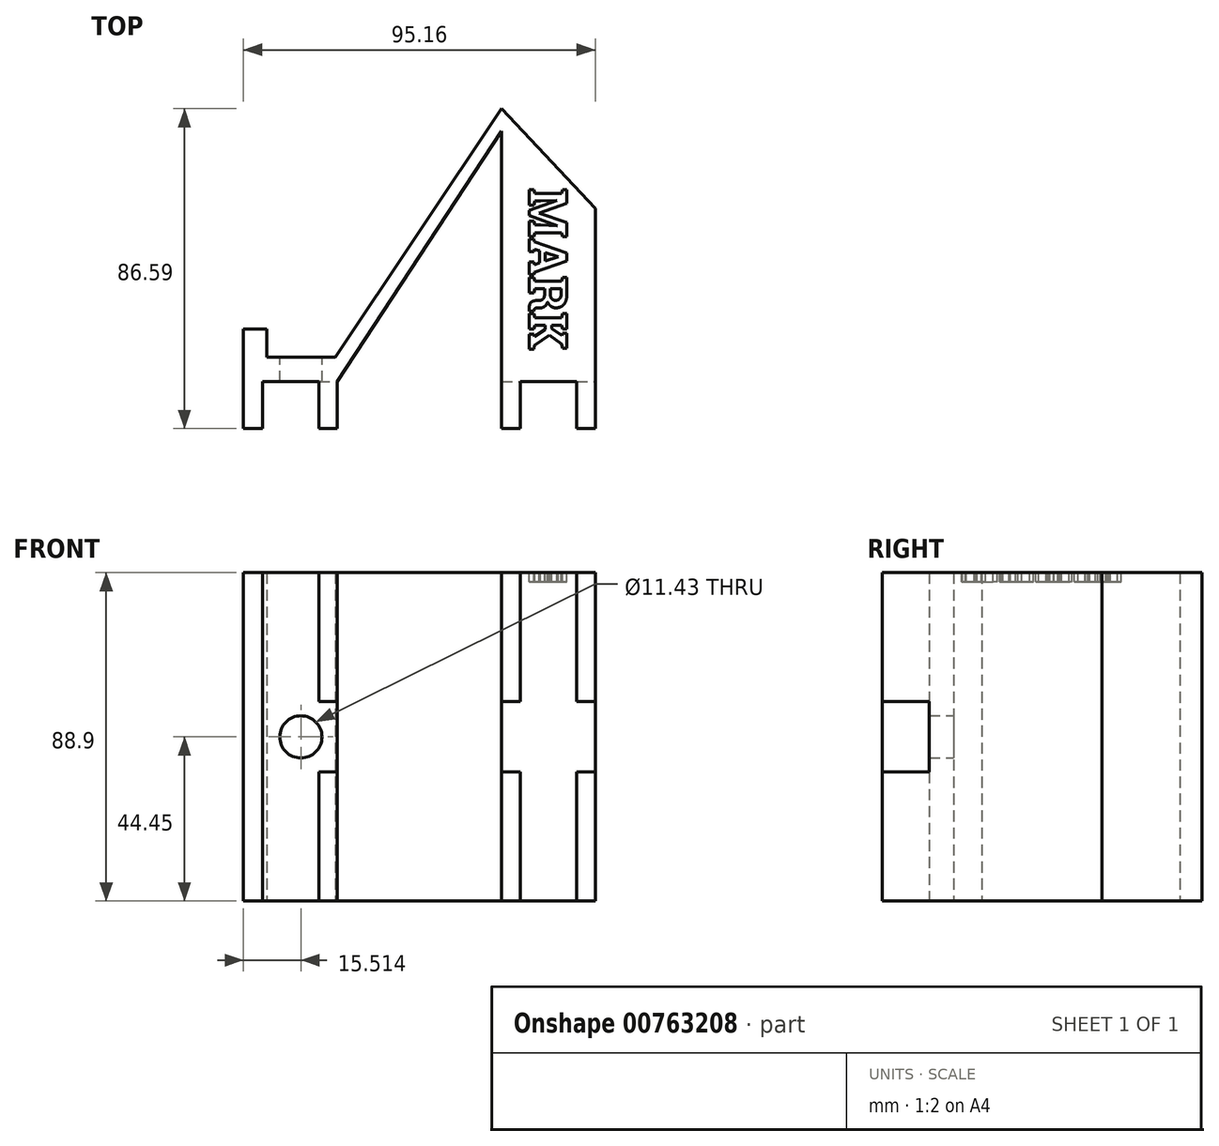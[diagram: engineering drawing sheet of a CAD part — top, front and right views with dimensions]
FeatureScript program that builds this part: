
annotation { "Feature Type Name" : "Feature", "Feature Type Description" : "" }
export const myFeature = defineFeature(function(context is Context, id is Id, definition is map)
    precondition{}
    {
        {
            var Q0;
            Q0=qCreatedBy(makeId("Top.planeOp"),FACE);
            var sketch = newSketch(context, id + "F0", { "sketchPlane" : qUnion([Q0])});
            skLineSegment(sketch, "E0.bottom", {"start": v(0, 0) * mm, "end": v(25.4, 0) * mm});
            skLineSegment(sketch, "E0.top", {"start": v(0, -46.85) * mm, "end": v(25.4, -46.85) * mm});
            skLineSegment(sketch, "E0.left", {"start": v(0, 0) * mm, "end": v(0, -46.85) * mm});
            skLineSegment(sketch, "E0.right", {"start": v(25.4, 0) * mm, "end": v(25.4, -46.85) * mm});
            skLineSegment(sketch, "E1", {"start": v(25.4, 0) * mm, "end": v(0, 27.04) * mm});
            skLineSegment(sketch, "E2", {"start": v(0, 27.04) * mm, "end": v(0, 0) * mm});
            skLineSegment(sketch, "E3", {"start": v(0, 27.04) * mm, "end": v(-49.44, -46.85) * mm});
            skLineSegment(sketch, "E4", {"start": v(-49.44, -46.85) * mm, "end": v(-44.36, -46.85) * mm});
            skLineSegment(sketch, "E5", {"start": v(-44.36, -46.85) * mm, "end": v(0, 21) * mm});
            skLineSegment(sketch, "E6", {"start": v(-45, -40.2) * mm, "end": v(-69.76, -40.2) * mm});
            skLineSegment(sketch, "E7", {"start": v(-69.76, -40.2) * mm, "end": v(-69.76, -46.85) * mm});
            skLineSegment(sketch, "E8", {"start": v(-69.76, -46.85) * mm, "end": v(-44.36, -46.85) * mm});
            skLineSegment(sketch, "E9", {"start": v(-69.76, -40.2) * mm, "end": v(-69.76, -32.58) * mm});
            skLineSegment(sketch, "E10", {"start": v(-69.76, -32.58) * mm, "end": v(-63.5, -32.58) * mm});
            skLineSegment(sketch, "E11", {"start": v(-63.5, -32.58) * mm, "end": v(-63.5, -40.2) * mm});
            skLineSegment(sketch, "E12", {"start": v(-69.76, -46.85) * mm, "end": v(-69.76, -59.55) * mm});
            skLineSegment(sketch, "E13", {"start": v(-69.76, -59.55) * mm, "end": v(-64.68, -59.55) * mm});
            skLineSegment(sketch, "E14", {"start": v(-64.68, -59.55) * mm, "end": v(-64.68, -46.85) * mm});
            skLineSegment(sketch, "E15", {"start": v(-49.44, -46.85) * mm, "end": v(-49.44, -59.55) * mm});
            skLineSegment(sketch, "E16", {"start": v(-49.44, -59.55) * mm, "end": v(-44.36, -59.55) * mm});
            skLineSegment(sketch, "E17", {"start": v(-44.36, -59.55) * mm, "end": v(-44.36, -46.85) * mm});
            skLineSegment(sketch, "E18", {"start": v(0, -46.85) * mm, "end": v(0, -59.55) * mm});
            skLineSegment(sketch, "E19", {"start": v(0, -59.55) * mm, "end": v(5.08, -59.55) * mm});
            skLineSegment(sketch, "E20", {"start": v(5.08, -59.55) * mm, "end": v(5.08, -46.85) * mm});
            skLineSegment(sketch, "E21", {"start": v(25.4, -59.55) * mm, "end": v(20.32, -59.55) * mm});
            skLineSegment(sketch, "E22", {"start": v(20.32, -59.55) * mm, "end": v(20.32, -46.85) * mm});
            skLineSegment(sketch, "E23", {"start": v(25.4, -59.55) * mm, "end": v(25.4, -46.85) * mm});
            skSolve(sketch);
        }
        {
            var Q0;
            Q0 = qSketchRegion(id + "F0", true);
            extrude(context, id + "F1", {"entities" : qUnion([Q0]), "depth" : 88.9 * mm, "offsetDistance" : 25.4 * mm});
        }
        {
            var Q0;
            Q0=makeQuery(id+"F1.opExtrude","SWEPT_FACE",FACE,{"disambiguationData":[OSD([sQuery(id+"F0.wireOp",EDGE,"E6")])]});
            var sketch = newSketch(context, id + "F2", { "sketchPlane" : qUnion([Q0])});
            skLineSegment(sketch, "E24", {"start": v(45, 44.45) * mm, "end": v(63.5, 44.45) * mm, "construction": true});
            skLineSegment(sketch, "E25", {"start": v(54.25, 0) * mm, "end": v(54.25, 88.9) * mm, "construction": true});
            skCircle(sketch, "E26", {"center": v(54.25, 44.45) * mm, "radius": 5.72 * mm});
            skSolve(sketch);
        }
        {
            var Q0;
            Q0 = qSketchRegion(id + "F2", true);
            extrude(context, id + "F3", {"entities" : qUnion([Q0]), "operationType" : NewBodyOperationType.REMOVE, "oppositeDirection" : true, "depth" : 7.62 * mm, "offsetDistance" : 25.4 * mm});
        }
        {
            var Q0;
            Q0=makeQuery(id+"F1.opExtrude","SWEPT_FACE",FACE,{"disambiguationData":[OSD([sQuery(id+"F0.wireOp",EDGE,"E0.right"),sQuery(id+"F0.wireOp",EDGE,"E23")])]});
            var sketch = newSketch(context, id + "F4", { "sketchPlane" : qUnion([Q0])});
            skPoint(sketch, "E27.startSnap0", {"position": v(0, 44.45) * mm});
            skLineSegment(sketch, "E28", {"start": v(-29.77, 88.9) * mm, "end": v(-29.77, 0) * mm, "construction": true});
            skLineSegment(sketch, "E29.bottom", {"start": v(-59.55, 53.98) * mm, "end": v(-46.85, 53.98) * mm});
            skLineSegment(sketch, "E29.top", {"start": v(-59.55, 34.93) * mm, "end": v(-46.85, 34.93) * mm});
            skLineSegment(sketch, "E29.left", {"start": v(-59.55, 53.98) * mm, "end": v(-59.55, 34.93) * mm});
            skLineSegment(sketch, "E29.right", {"start": v(-46.85, 53.98) * mm, "end": v(-46.85, 34.93) * mm});
            skPoint(sketch, "E30", {"position": v(-46.85, 44.45) * mm});
            skLineSegment(sketch, "E31", {"start": v(-59.55, 53.98) * mm, "end": v(-59.55, 88.9) * mm, "construction": true});
            skLineSegment(sketch, "E32", {"start": v(-59.55, 34.93) * mm, "end": v(-59.55, 0) * mm, "construction": true});
            skPoint(sketch, "E27.end.orphan", {"position": v(-59.55, 44.45) * mm});
            skPoint(sketch, "E27.start.orphan", {"position": v(-57.69, 44.45) * mm});
            skSolve(sketch);
        }
        {
            var Q0;
            Q0=makeQuery(id+"F4.imprint","IMPRINT",FACE,{"disambiguationData":[TD([[makeQuery(id+"F4.imprint","IMPRINT",EDGE,{"derivedFrom":sQuery(id+"F4.wireOp",EDGE,"E29.bottom")}),-1.0]])]});
            extrude(context, id + "F5", {"entities" : qUnion([Q0]), "operationType" : NewBodyOperationType.REMOVE, "oppositeDirection" : true, "depth" : 82.55 * mm, "offsetDistance" : 25.4 * mm});
        }
        {
            var Q0;
            Q0=makeQuery(id+"F1.opExtrude","CAP_FACE",FACE,{"disambiguationData":[OSD([sQuery(id+"F0.wireOp",EDGE,"E0.top"),sQuery(id+"F0.wireOp",EDGE,"E0.left"),sQuery(id+"F0.wireOp",EDGE,"E0.right"),sQuery(id+"F0.wireOp",EDGE,"E1"),sQuery(id+"F0.wireOp",EDGE,"E2"),sQuery(id+"F0.wireOp",EDGE,"E3"),sQuery(id+"F0.wireOp",EDGE,"E5"),sQuery(id+"F0.wireOp",EDGE,"E6"),sQuery(id+"F0.wireOp",EDGE,"E7"),sQuery(id+"F0.wireOp",EDGE,"E8"),sQuery(id+"F0.wireOp",EDGE,"E9"),sQuery(id+"F0.wireOp",EDGE,"E10"),sQuery(id+"F0.wireOp",EDGE,"E11"),sQuery(id+"F0.wireOp",EDGE,"E12"),sQuery(id+"F0.wireOp",EDGE,"E13"),sQuery(id+"F0.wireOp",EDGE,"E14"),sQuery(id+"F0.wireOp",EDGE,"E15"),sQuery(id+"F0.wireOp",EDGE,"E16"),sQuery(id+"F0.wireOp",EDGE,"E17"),sQuery(id+"F0.wireOp",EDGE,"E18"),sQuery(id+"F0.wireOp",EDGE,"E19"),sQuery(id+"F0.wireOp",EDGE,"E20"),sQuery(id+"F0.wireOp",EDGE,"E21"),sQuery(id+"F0.wireOp",EDGE,"E22"),sQuery(id+"F0.wireOp",EDGE,"E23")])],"isStart":false});
            var sketch = newSketch(context, id + "F6", { "sketchPlane" : qUnion([Q0])});
            skPoint(sketch, "E33", {"position": v(12.7, -16.66) * mm});
            skText(sketch, "E34", { "text": "MARK", "fontName": "RobotoSlab-Bold.ttf"});
            skLineSegment(sketch, "E35", {"start": v(12.7, -46.85) * mm, "end": v(12.7, 13.52) * mm, "construction": true});
            const initialGuessF6  = {"E34": [0.00755, 0.00556, 0, -1, 0.0103]};
            skSetInitialGuess(sketch, initialGuessF6);
            skSolve(sketch);
        }
        {
            var Q0;
            Q0 = qSketchRegion(id + "F6", true);
            extrude(context, id + "F7", {"entities" : qUnion([Q0]), "operationType" : NewBodyOperationType.REMOVE, "oppositeDirection" : true, "depth" : 2.54 * mm, "offsetDistance" : 25.4 * mm});
        }
    });
